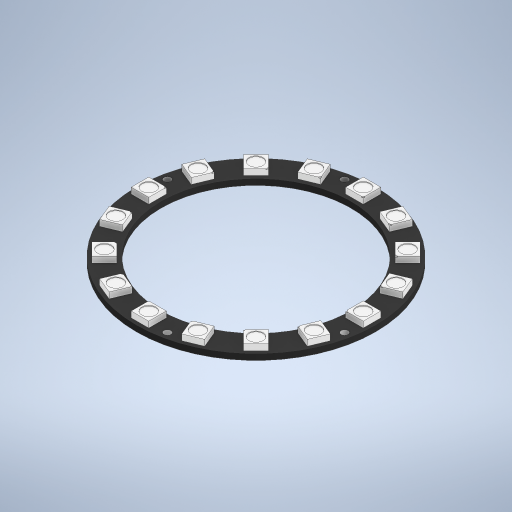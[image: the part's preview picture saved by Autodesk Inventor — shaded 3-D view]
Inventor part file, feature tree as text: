
AUTODESK INVENTOR PART (.ipt)
format: ipt  version: 2023 (Build 270158000, 158)  size: 448,512 bytes
history: native  units: mm
features: extrude x5, sketch x4, pattern_circular x2, other x1, projected_geometry x1
ambient origin geometry x8: Origin, YZ Plane, XZ Plane, XY Plane, X Axis, Y Axis, Z Axis, Center Point
bodies: Body1 (feature_tree)
feature tree (13):
  other  "솔리드1"
  sketch  "스케치2"
  extrude  "돌출1"  Depth=68.0mm
  extrude  "돌출2"  Depth=54.0mm
  extrude  "돌출3"  Depth=5.0mm
  pattern_circular  "원형 패턴1"  [2 undecoded]
  extrude  "돌출4"  Depth=33.0mm
  extrude  "돌출5"  Depth=1.7mm TaperAngle=0.0deg
  pattern_circular  "원형 패턴2"  [2 undecoded]
  sketch  "스케치3"
  projected_geometry  "투영된 루프1"
  sketch  "스케치4"
  sketch  "스케치5"
note: 4 required parameter values undecoded (feature->parameter linkage not recoverable at this tier; creation-order binding heuristic only, values carry confidence <= 0.55)
